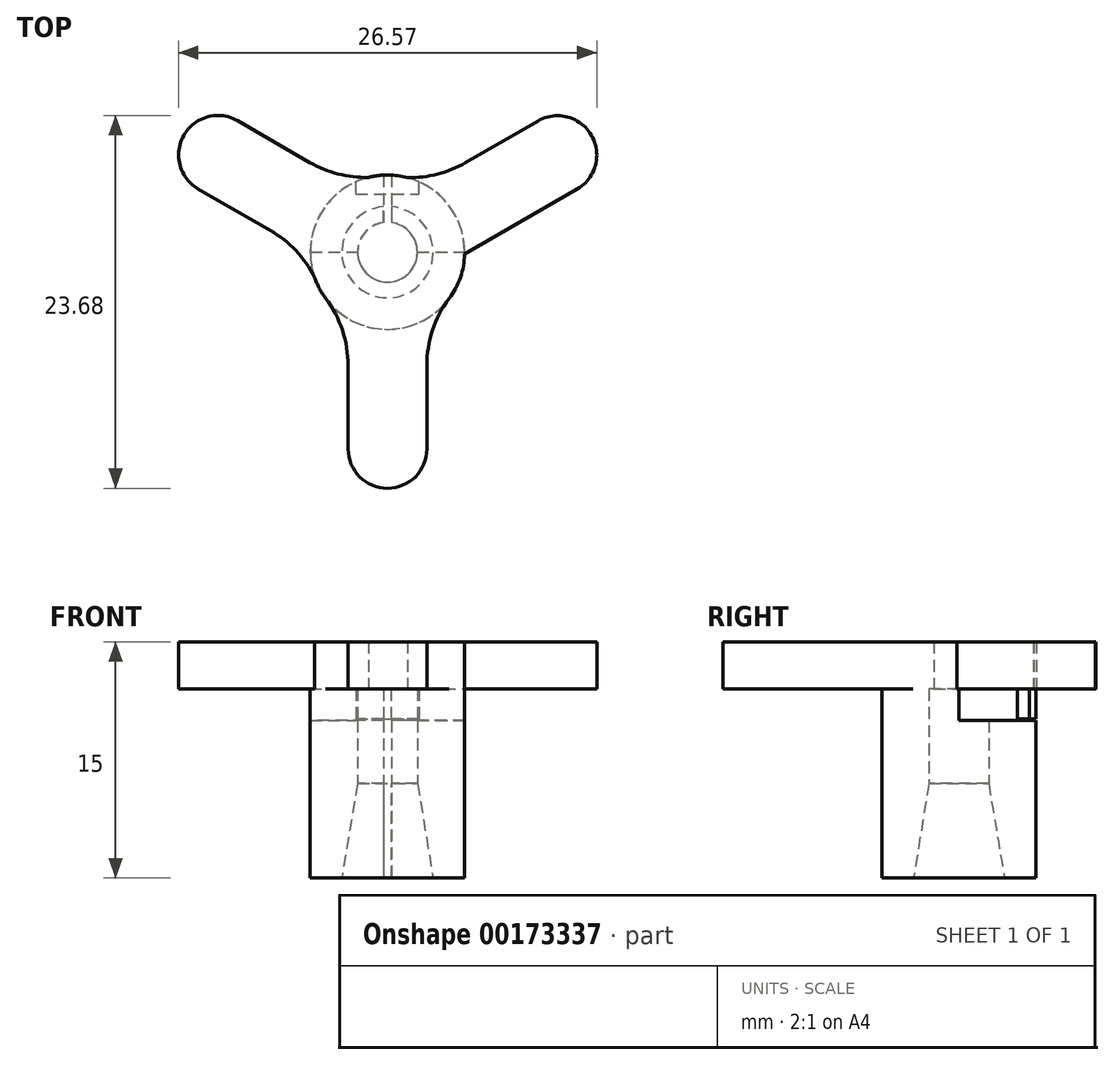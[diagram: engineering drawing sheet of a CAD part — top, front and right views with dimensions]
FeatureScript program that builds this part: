
annotation { "Feature Type Name" : "Feature", "Feature Type Description" : "" }
export const myFeature = defineFeature(function(context is Context, id is Id, definition is map)
    precondition{}
    {
        {
            var Q0;
            Q0=qCreatedBy(makeId("Top.planeOp"),FACE);
            var sketch = newSketch(context, id + "F0", { "sketchPlane" : qUnion([Q0])});
            skCircle(sketch, "E0", {"center": v(0, 0) * mm, "radius": 1.9 * mm});
            skCircle(sketch, "E1", {"center": v(0, 0) * mm, "radius": 4.9 * mm});
            skLineSegment(sketch, "E2", {"start": v(-0.25, 4.9) * mm, "end": v(0.25, 4.9) * mm});
            skPoint(sketch, "E3", {"position": v(0, 4.9) * mm});
            skLineSegment(sketch, "E4", {"start": v(-0.25, 4.9) * mm, "end": v(-0.25, 1.88) * mm});
            skLineSegment(sketch, "E5", {"start": v(0.25, 4.9) * mm, "end": v(0.25, 1.88) * mm});
            skSolve(sketch);
        }
        {
            var Q0;
            {var subQ0=sQuery(id+"F0.wireOp",EDGE,"E4");var subQ1=sQuery(id+"F0.wireOp",EDGE,"E0");var subQ2=makeQuery(id+"F0.imprint","INTERSECT",VERTEX,{"derivedFrom":[subQ1,subQ0]});Q0=makeQuery(id+"F0.imprint","IMPRINT",FACE,{"disambiguationData":[TD([[makeQuery(id+"F0.imprint","IMPRINT",EDGE,{"disambiguationData":[TD([[subQ2,-1.0]])],"derivedFrom":subQ1}),-1.0]])]});}
            extrude(context, id + "F1", {"entities" : qUnion([Q0]), "depth" : 10 * mm});
        }
        {
            var Q0;
            Q0=makeQuery(id+"F1.opExtrude","CAP_FACE",FACE,{"disambiguationData":[OSD([sQuery(id+"F0.wireOp",EDGE,"E0"),sQuery(id+"F0.wireOp",EDGE,"E1"),sQuery(id+"F0.wireOp",EDGE,"E4"),sQuery(id+"F0.wireOp",EDGE,"E5")])],"isStart":false});
            var sketch = newSketch(context, id + "F2", { "sketchPlane" : qUnion([Q0])});
            skArc(sketch, "E6", {"start": v(-4.9, 0) * mm, "mid": v(0, -4.9) * mm, "end": v(4.9, 0) * mm});
            skLineSegment(sketch, "E7", {"start": v(-4.9, 0) * mm, "end": v(4.9, 0) * mm});
            skCircle(sketch, "E8", {"center": v(0, 0) * mm, "radius": 1.9 * mm});
            skSolve(sketch);
        }
        {
            var Q0;
            {var subQ0=sQuery(id+"F2.wireOp",EDGE,"E6");Q0=makeQuery(id+"F2.imprint","IMPRINT",FACE,{"disambiguationData":[TD([[makeQuery(id+"F2.imprint","IMPRINT",EDGE,{"derivedFrom":subQ0}),1.0]])]});}
            extrude(context, id + "F3", {"entities" : qUnion([Q0]), "operationType" : NewBodyOperationType.ADD, "depth" : 2 * mm});
        }
        {
            var Q0;
            Q0=makeQuery(id+"F3.opExtrude","CAP_FACE",FACE,{"disambiguationData":[OSD([sQuery(id+"F2.wireOp",EDGE,"E6"),sQuery(id+"F2.wireOp",EDGE,"E7"),sQuery(id+"F2.wireOp",EDGE,"E8")])],"isStart":false});
            var sketch = newSketch(context, id + "F4", { "sketchPlane" : qUnion([Q0])});
            skCircle(sketch, "E9", {"center": v(0, 0) * mm, "radius": 4.9 * mm});
            skCircle(sketch, "E10", {"center": v(0, 0) * mm, "radius": 15 * mm});
            skArc(sketch, "E11", {"start": v(-2.5, -12.5) * mm, "mid": v(0, -15) * mm, "end": v(2.5, -12.5) * mm});
            skLineSegment(sketch, "E12", {"start": v(-2.5, -12.5) * mm, "end": v(-2.5, -4.21) * mm});
            skLineSegment(sketch, "E13", {"start": v(2.5, -12.5) * mm, "end": v(2.5, -4.21) * mm});
            skArc(sketch, "E14", {"start": v(-2.5, -7.21) * mm, "mid": v(-2.87, -4.96) * mm, "end": v(-3.92, -2.94) * mm});
            skArc(sketch, "E15", {"start": v(3.92, -2.94) * mm, "mid": v(2.87, -4.96) * mm, "end": v(2.5, -7.21) * mm});
            skArc(sketch, "E16.1.0", {"start": v(12.05, 4) * mm, "mid": v(12.96, 7.42) * mm, "end": v(9.55, 8.33) * mm});
            skLineSegment(sketch, "E16.1.1", {"start": v(9.55, 8.33) * mm, "end": v(2.37, 4.19) * mm});
            skLineSegment(sketch, "E16.1.2", {"start": v(12.05, 4) * mm, "end": v(4.87, -0.14) * mm});
            skArc(sketch, "E16.1.3", {"start": v(7.47, 1.36) * mm, "mid": v(5.7, -0.09) * mm, "end": v(4.47, -2.01) * mm});
            skArc(sketch, "E16.1.4", {"start": v(0.55, 4.78) * mm, "mid": v(2.83, 4.88) * mm, "end": v(4.97, 5.69) * mm});
            skArc(sketch, "E16.2.0", {"start": v(-9.52, 8.35) * mm, "mid": v(-12.93, 7.43) * mm, "end": v(-12.02, 4.02) * mm});
            skLineSegment(sketch, "E16.2.1", {"start": v(-12.02, 4.02) * mm, "end": v(-4.84, -0.13) * mm});
            skLineSegment(sketch, "E16.2.2", {"start": v(-9.52, 8.35) * mm, "end": v(-2.34, 4.2) * mm});
            skArc(sketch, "E16.2.3", {"start": v(-4.94, 5.7) * mm, "mid": v(-2.8, 4.9) * mm, "end": v(-0.52, 4.8) * mm});
            skArc(sketch, "E16.2.4", {"start": v(-4.45, -2) * mm, "mid": v(-5.67, -0.07) * mm, "end": v(-7.44, 1.37) * mm});
            skPoint(sketch, "E16.center", {"position": v(0, -0.05) * mm});
            skSolve(sketch);
        }
        {
            var Q0;
            {var subQ6=sQuery(id+"F2.wireOp",EDGE,"E8");Q0=makeQuery(id+"F4.imprint","IMPRINT",FACE,{"disambiguationData":[TD([[makeQuery(id+"F4.imprint","IMPRINT",EDGE,{"derivedFrom":makeQuery(id+"F3.opExtrude","CAP_EDGE",EDGE,{"disambiguationData":[OSD([subQ6])],"isStart":false})}),-1.0]])]});}
            var Q1;
            {var subQ8=sQuery(id+"F2.wireOp",EDGE,"E8");Q1=makeQuery(id+"F4.imprint","IMPRINT",FACE,{"disambiguationData":[TD([[makeQuery(id+"F4.imprint","IMPRINT",EDGE,{"derivedFrom":makeQuery(id+"F3.opExtrude","CAP_EDGE",EDGE,{"disambiguationData":[OSD([subQ8])],"isStart":false})}),1.0]])]});}
            var Q2;
            {var subQ0=sQuery(id+"F4.wireOp",EDGE,"9c31c9c1-0bcc-4ed4-a2f3-30294d7c124c.1.1");Q2=makeQuery(id+"F4.imprint","IMPRINT",FACE,{"disambiguationData":[TD([[makeQuery(id+"F4.imprint","IMPRINT",EDGE,{"derivedFrom":subQ0}),-1.0]])]});}
            var Q3;
            {var subQ0=sQuery(id+"F4.wireOp",EDGE,"9c31c9c1-0bcc-4ed4-a2f3-30294d7c124c.1.0");var subQ1=makeQuery(id+"F4.imprint","INTERSECT",VERTEX,{"derivedFrom":[subQ0,sQuery(id+"F4.wireOp",EDGE,"9c31c9c1-0bcc-4ed4-a2f3-30294d7c124c.1.2")]});Q3=makeQuery(id+"F4.imprint","IMPRINT",FACE,{"disambiguationData":[TD([[makeQuery(id+"F4.imprint","IMPRINT",EDGE,{"disambiguationData":[TD([[subQ1,-1.0]])],"derivedFrom":subQ0}),1.0]])]});}
            var Q4;
            {var subQ0=sQuery(id+"F4.wireOp",EDGE,"STuvLVaa-MU8C-Dhbz-SaFo-3KpY4SZEZLty");var subQ1=makeQuery(id+"F4.imprint","INTERSECT",VERTEX,{"derivedFrom":[subQ0,sQuery(id+"F4.wireOp",EDGE,"ktpVrwZ7-m0nx-2aj5-DfaQ-GeAfub4Ecsry")]});Q4=makeQuery(id+"F4.imprint","IMPRINT",FACE,{"disambiguationData":[TD([[makeQuery(id+"F4.imprint","IMPRINT",EDGE,{"disambiguationData":[TD([[subQ1,-1.0]])],"derivedFrom":subQ0}),1.0]])]});}
            var Q5;
            {var subQ0=sQuery(id+"F4.wireOp",EDGE,"fXAfpD2b-S489-TMEU-ql5s-tNgI2AmWdHs7");Q5=makeQuery(id+"F4.imprint","IMPRINT",FACE,{"disambiguationData":[TD([[makeQuery(id+"F4.imprint","IMPRINT",EDGE,{"derivedFrom":subQ0}),-1.0]])]});}
            var Q6;
            {var subQ0=sQuery(id+"F4.wireOp",EDGE,"9c31c9c1-0bcc-4ed4-a2f3-30294d7c124c.4.1");Q6=makeQuery(id+"F4.imprint","IMPRINT",FACE,{"disambiguationData":[TD([[makeQuery(id+"F4.imprint","IMPRINT",EDGE,{"derivedFrom":subQ0}),-1.0]])]});}
            var Q7;
            {var subQ0=sQuery(id+"F4.wireOp",EDGE,"9c31c9c1-0bcc-4ed4-a2f3-30294d7c124c.4.0");var subQ1=makeQuery(id+"F4.imprint","INTERSECT",VERTEX,{"derivedFrom":[subQ0,sQuery(id+"F4.wireOp",EDGE,"9c31c9c1-0bcc-4ed4-a2f3-30294d7c124c.4.2")]});Q7=makeQuery(id+"F4.imprint","IMPRINT",FACE,{"disambiguationData":[TD([[makeQuery(id+"F4.imprint","IMPRINT",EDGE,{"disambiguationData":[TD([[subQ1,-1.0]])],"derivedFrom":subQ0}),1.0]])]});}
            var Q8;
            {var subQ0=sQuery(id+"F4.wireOp",EDGE,"9c31c9c1-0bcc-4ed4-a2f3-30294d7c124c.3.0");var subQ1=makeQuery(id+"F4.imprint","INTERSECT",VERTEX,{"derivedFrom":[subQ0,sQuery(id+"F4.wireOp",EDGE,"9c31c9c1-0bcc-4ed4-a2f3-30294d7c124c.3.2")]});Q8=makeQuery(id+"F4.imprint","IMPRINT",FACE,{"disambiguationData":[TD([[makeQuery(id+"F4.imprint","IMPRINT",EDGE,{"disambiguationData":[TD([[subQ1,-1.0]])],"derivedFrom":subQ0}),1.0]])]});}
            var Q9;
            {var subQ0=sQuery(id+"F4.wireOp",EDGE,"9c31c9c1-0bcc-4ed4-a2f3-30294d7c124c.2.1");Q9=makeQuery(id+"F4.imprint","IMPRINT",FACE,{"disambiguationData":[TD([[makeQuery(id+"F4.imprint","IMPRINT",EDGE,{"derivedFrom":subQ0}),-1.0]])]});}
            var Q10;
            {var subQ0=sQuery(id+"F4.wireOp",EDGE,"9c31c9c1-0bcc-4ed4-a2f3-30294d7c124c.2.0");var subQ1=makeQuery(id+"F4.imprint","INTERSECT",VERTEX,{"derivedFrom":[subQ0,sQuery(id+"F4.wireOp",EDGE,"9c31c9c1-0bcc-4ed4-a2f3-30294d7c124c.2.2")]});Q10=makeQuery(id+"F4.imprint","IMPRINT",FACE,{"disambiguationData":[TD([[makeQuery(id+"F4.imprint","IMPRINT",EDGE,{"disambiguationData":[TD([[subQ1,-1.0]])],"derivedFrom":subQ0}),1.0]])]});}
            var Q11;
            {var subQ0=sQuery(id+"F4.wireOp",EDGE,"9c31c9c1-0bcc-4ed4-a2f3-30294d7c124c.3.1");Q11=makeQuery(id+"F4.imprint","IMPRINT",FACE,{"disambiguationData":[TD([[makeQuery(id+"F4.imprint","IMPRINT",EDGE,{"derivedFrom":subQ0}),-1.0]])]});}
            var Q12;
            {var subQ4=sQuery(id+"F4.wireOp",EDGE,"45d453c9-bf6c-4dbd-8a0c-38babedebff1.1.0");Q12=makeQuery(id+"F4.imprint","IMPRINT",FACE,{"disambiguationData":[TD([[makeQuery(id+"F4.imprint","IMPRINT",EDGE,{"derivedFrom":subQ4}),-1.0]])]});}
            var Q13;
            {var subQ0=sQuery(id+"F4.wireOp",EDGE,"45d453c9-bf6c-4dbd-8a0c-38babedebff1.1.2");var subQ1=makeQuery(id+"F4.imprint","INTERSECT",VERTEX,{"derivedFrom":[sQuery(id+"F4.wireOp",EDGE,"45d453c9-bf6c-4dbd-8a0c-38babedebff1.1.1"),subQ0]});Q13=makeQuery(id+"F4.imprint","IMPRINT",FACE,{"disambiguationData":[TD([[makeQuery(id+"F4.imprint","IMPRINT",EDGE,{"disambiguationData":[TD([[subQ1,-1.0]])],"derivedFrom":subQ0}),1.0]])]});}
            var Q14;
            {var subQ0=sQuery(id+"F4.wireOp",EDGE,"45d453c9-bf6c-4dbd-8a0c-38babedebff1.4.0");Q14=makeQuery(id+"F4.imprint","IMPRINT",FACE,{"disambiguationData":[TD([[makeQuery(id+"F4.imprint","IMPRINT",EDGE,{"derivedFrom":subQ0}),-1.0]])]});}
            var Q15;
            {var subQ0=sQuery(id+"F4.wireOp",EDGE,"45d453c9-bf6c-4dbd-8a0c-38babedebff1.4.2");var subQ1=makeQuery(id+"F4.imprint","INTERSECT",VERTEX,{"derivedFrom":[sQuery(id+"F4.wireOp",EDGE,"45d453c9-bf6c-4dbd-8a0c-38babedebff1.4.1"),subQ0]});Q15=makeQuery(id+"F4.imprint","IMPRINT",FACE,{"disambiguationData":[TD([[makeQuery(id+"F4.imprint","IMPRINT",EDGE,{"disambiguationData":[TD([[subQ1,-1.0]])],"derivedFrom":subQ0}),1.0]])]});}
            var Q16;
            {var subQ0=sQuery(id+"F4.wireOp",EDGE,"45d453c9-bf6c-4dbd-8a0c-38babedebff1.3.0");Q16=makeQuery(id+"F4.imprint","IMPRINT",FACE,{"disambiguationData":[TD([[makeQuery(id+"F4.imprint","IMPRINT",EDGE,{"derivedFrom":subQ0}),-1.0]])]});}
            var Q17;
            {var subQ0=sQuery(id+"F4.wireOp",EDGE,"45d453c9-bf6c-4dbd-8a0c-38babedebff1.3.2");var subQ1=makeQuery(id+"F4.imprint","INTERSECT",VERTEX,{"derivedFrom":[sQuery(id+"F4.wireOp",EDGE,"45d453c9-bf6c-4dbd-8a0c-38babedebff1.3.1"),subQ0]});Q17=makeQuery(id+"F4.imprint","IMPRINT",FACE,{"disambiguationData":[TD([[makeQuery(id+"F4.imprint","IMPRINT",EDGE,{"disambiguationData":[TD([[subQ1,-1.0]])],"derivedFrom":subQ0}),1.0]])]});}
            var Q18;
            {var subQ0=sQuery(id+"F4.wireOp",EDGE,"45d453c9-bf6c-4dbd-8a0c-38babedebff1.2.0");Q18=makeQuery(id+"F4.imprint","IMPRINT",FACE,{"disambiguationData":[TD([[makeQuery(id+"F4.imprint","IMPRINT",EDGE,{"derivedFrom":subQ0}),-1.0]])]});}
            var Q19;
            {var subQ0=sQuery(id+"F4.wireOp",EDGE,"45d453c9-bf6c-4dbd-8a0c-38babedebff1.2.2");var subQ1=makeQuery(id+"F4.imprint","INTERSECT",VERTEX,{"derivedFrom":[sQuery(id+"F4.wireOp",EDGE,"45d453c9-bf6c-4dbd-8a0c-38babedebff1.2.1"),subQ0]});Q19=makeQuery(id+"F4.imprint","IMPRINT",FACE,{"disambiguationData":[TD([[makeQuery(id+"F4.imprint","IMPRINT",EDGE,{"disambiguationData":[TD([[subQ1,-1.0]])],"derivedFrom":subQ0}),1.0]])]});}
            var Q20;
            {var subQ0=sQuery(id+"F4.wireOp",EDGE,"E16.2.2");var subQ1=sQuery(id+"F4.wireOp",EDGE,"E16.2.0");var subQ2=makeQuery(id+"F4.imprint","INTERSECT",VERTEX,{"derivedFrom":[subQ1,subQ0]});Q20=makeQuery(id+"F4.imprint","IMPRINT",FACE,{"disambiguationData":[TD([[makeQuery(id+"F4.imprint","IMPRINT",EDGE,{"disambiguationData":[TD([[subQ2,-1.0]])],"derivedFrom":subQ1}),1.0]])]});}
            var Q21;
            {var subQ0=sQuery(id+"F4.wireOp",EDGE,"E16.1.2");var subQ1=sQuery(id+"F4.wireOp",EDGE,"E16.1.0");var subQ2=makeQuery(id+"F4.imprint","INTERSECT",VERTEX,{"derivedFrom":[subQ1,subQ0]});Q21=makeQuery(id+"F4.imprint","IMPRINT",FACE,{"disambiguationData":[TD([[makeQuery(id+"F4.imprint","IMPRINT",EDGE,{"disambiguationData":[TD([[subQ2,-1.0]])],"derivedFrom":subQ1}),1.0]])]});}
            var Q22;
            {var subQ5=sQuery(id+"F4.wireOp",EDGE,"E12");var subQ8=sQuery(id+"F4.wireOp",EDGE,"E9");var subQ9=makeQuery(id+"F4.imprint","INTERSECT",VERTEX,{"derivedFrom":[subQ8,subQ5]});Q22=makeQuery(id+"F4.imprint","IMPRINT",FACE,{"disambiguationData":[TD([[makeQuery(id+"F4.imprint","IMPRINT",EDGE,{"disambiguationData":[TD([[subQ9,-1.0]])],"derivedFrom":subQ8}),-1.0]])]});}
            var Q23;
            {var subQ3=sQuery(id+"F4.wireOp",EDGE,"E14");Q23=makeQuery(id+"F4.imprint","IMPRINT",FACE,{"disambiguationData":[TD([[makeQuery(id+"F4.imprint","IMPRINT",EDGE,{"derivedFrom":subQ3}),-1.0]])]});}
            var Q24;
            {var subQ3=sQuery(id+"F4.wireOp",EDGE,"E16.2.4");Q24=makeQuery(id+"F4.imprint","IMPRINT",FACE,{"disambiguationData":[TD([[makeQuery(id+"F4.imprint","IMPRINT",EDGE,{"derivedFrom":subQ3}),-1.0]])]});}
            var Q25;
            {var subQ3=sQuery(id+"F4.wireOp",EDGE,"E15");Q25=makeQuery(id+"F4.imprint","IMPRINT",FACE,{"disambiguationData":[TD([[makeQuery(id+"F4.imprint","IMPRINT",EDGE,{"derivedFrom":subQ3}),-1.0]])]});}
            var Q26;
            {var subQ3=sQuery(id+"F4.wireOp",EDGE,"E16.1.3");Q26=makeQuery(id+"F4.imprint","IMPRINT",FACE,{"disambiguationData":[TD([[makeQuery(id+"F4.imprint","IMPRINT",EDGE,{"derivedFrom":subQ3}),-1.0]])]});}
            var Q27;
            {var subQ3=sQuery(id+"F4.wireOp",EDGE,"E16.2.3");Q27=makeQuery(id+"F4.imprint","IMPRINT",FACE,{"disambiguationData":[TD([[makeQuery(id+"F4.imprint","IMPRINT",EDGE,{"derivedFrom":subQ3}),-1.0]])]});}
            var Q28;
            {var subQ3=sQuery(id+"F4.wireOp",EDGE,"E16.1.4");Q28=makeQuery(id+"F4.imprint","IMPRINT",FACE,{"disambiguationData":[TD([[makeQuery(id+"F4.imprint","IMPRINT",EDGE,{"derivedFrom":subQ3}),-1.0]])]});}
            extrude(context, id + "F5", {"entities" : qUnion([Q0, Q1, Q2, Q3, Q4, Q5, Q6, Q7, Q8, Q9, Q10, Q11, Q12, Q13, Q14, Q15, Q16, Q17, Q18, Q19, Q20, Q21, Q22, Q23, Q24, Q25, Q26, Q27, Q28]), "operationType" : NewBodyOperationType.ADD, "depth" : 3 * mm});
        }
        {
            var Q0;
            Q0=makeQuery(id+"F1.opExtrude","CAP_EDGE",EDGE,{"disambiguationData":[OSD([sQuery(id+"F0.wireOp",EDGE,"E0")])],"isStart":true});
            chamfer(context, id + "F6", {"entities" : qUnion([Q0]), "chamferType" : ChamferType.TWO_OFFSETS, "width1" : 1 * mm, "oppositeDirection" : false, "width2" : 6 * mm, "tangentPropagation" : true});
        }
        {
            var Q0;
            {var subQ1=sQuery(id+"F0.wireOp",EDGE,"E4");var subQ2=sQuery(id+"F0.wireOp",EDGE,"E1");var subQ3=sQuery(id+"F0.wireOp",EDGE,"E0");Q0=makeQuery(id+"F3.boolean.opBoolean","SPLIT",FACE,{"disambiguationData":[TD([makeQuery(id+"F1.opExtrude","SWEPT_FACE",FACE,{"disambiguationData":[OSD([subQ1])]})])],"derivedFrom":makeQuery(id+"F1.opExtrude","CAP_FACE",FACE,{"disambiguationData":[OSD([subQ3,subQ2,subQ1,sQuery(id+"F0.wireOp",EDGE,"E5")])],"isStart":false})});}
            var sketch = newSketch(context, id + "F7", { "sketchPlane" : qUnion([Q0])});
            skLineSegment(sketch, "E17.bottom", {"start": v(-2, 4.9) * mm, "end": v(2, 4.9) * mm});
            skLineSegment(sketch, "E17.top", {"start": v(-2, 3.7) * mm, "end": v(2, 3.7) * mm});
            skLineSegment(sketch, "E17.left", {"start": v(-2, 9.55) * mm, "end": v(-2, 3.7) * mm});
            skLineSegment(sketch, "E17.right", {"start": v(2, 9.55) * mm, "end": v(2, 3.7) * mm});
            skPoint(sketch, "E18", {"position": v(0, 4.9) * mm});
            skPoint(sketch, "E19", {"position": v(-0.25, 4.9) * mm});
            skPoint(sketch, "E20", {"position": v(0.24, 4.9) * mm});
            skArc(sketch, "E21", {"start": v(2, 4.47) * mm, "mid": v(1.14, 4.77) * mm, "end": v(0.24, 4.9) * mm});
            skPoint(sketch, "E22", {"position": v(1.14, 4.77) * mm});
            skSolve(sketch);
        }
        {
            var Q0;
            {var subQ0=sQuery(id+"F7.wireOp",EDGE,"E17.left");var subQ1=sQuery(id+"F7.wireOp",EDGE,"E17.top");var subQ2=makeQuery(id+"F7.imprint","INTERSECT",VERTEX,{"derivedFrom":[subQ1,subQ0]});Q0=makeQuery(id+"F7.imprint","IMPRINT",FACE,{"disambiguationData":[TD([[makeQuery(id+"F7.imprint","IMPRINT",EDGE,{"disambiguationData":[TD([[subQ2,-1.0]])],"derivedFrom":subQ1}),1.0]])]});}
            var Q1;
            {var subQ8=sQuery(id+"F7.wireOp",EDGE,"E17.right");var subQ10=sQuery(id+"F7.wireOp",EDGE,"E17.top");var subQ11=makeQuery(id+"F7.imprint","INTERSECT",VERTEX,{"derivedFrom":[subQ10,subQ8]});Q1=makeQuery(id+"F7.imprint","IMPRINT",FACE,{"disambiguationData":[TD([[makeQuery(id+"F7.imprint","IMPRINT",EDGE,{"disambiguationData":[TD([[subQ11,1.0]])],"derivedFrom":subQ10}),1.0]])]});}
            var Q2;
            {var subQ0=sQuery(id+"F4.wireOp",EDGE,"E14");var subQ1=sQuery(id+"F4.wireOp",EDGE,"E9");var subQ2=sQuery(id+"F4.wireOp",EDGE,"E16.2.4");var subQ3=sQuery(id+"F4.wireOp",EDGE,"E16.1.4");var subQ4=sQuery(id+"F4.wireOp",EDGE,"E16.2.3");var subQ5=sQuery(id+"F4.wireOp",EDGE,"E16.2.0");var subQ11=sQuery(id+"F4.wireOp",EDGE,"E16.1.1");var subQ12=sQuery(id+"F4.wireOp",EDGE,"E16.1.0");var subQ13=sQuery(id+"F4.wireOp",EDGE,"E15");var subQ14=sQuery(id+"F4.wireOp",EDGE,"E16.1.2");var subQ15=sQuery(id+"F4.wireOp",EDGE,"E16.2.1");var subQ16=sQuery(id+"F4.wireOp",EDGE,"E16.2.2");Q2=makeQuery(id+"F5.boolean.opBoolean","SPLIT",FACE,{"disambiguationData":[TD([makeQuery(id+"F1.opExtrude","SWEPT_FACE",FACE,{"disambiguationData":[OSD([sQuery(id+"F0.wireOp",EDGE,"E0")])]})])],"derivedFrom":makeQuery(id+"F5.opExtrude","CAP_FACE",FACE,{"disambiguationData":[OSD([subQ1,sQuery(id+"F4.wireOp",EDGE,"E11"),sQuery(id+"F4.wireOp",EDGE,"E12"),sQuery(id+"F4.wireOp",EDGE,"E13"),subQ0,subQ13,subQ12,subQ11,subQ14,subQ3,subQ5,subQ15,subQ16,subQ4,subQ2])],"isStart":true})});}
            extrude(context, id + "F8", {"entities" : qUnion([Q0, Q1]), "operationType" : NewBodyOperationType.ADD, "endBound" : BoundingType.UP_TO_SURFACE, "endBoundEntityFace" : qUnion([Q2]), "depth" : 25 * mm});
        }
        {
            var Q0;
            Q0=makeQuery(id+"F8.opExtrude","SWEPT_FACE",FACE,{"disambiguationData":[OSD([sQuery(id+"F7.wireOp",EDGE,"E17.bottom")])]});
            var sketch = newSketch(context, id + "F9", { "sketchPlane" : qUnion([Q0])});
            skLineSegment(sketch, "E23.bottom", {"start": v(2, 10.1) * mm, "end": v(-2, 10.1) * mm});
            skLineSegment(sketch, "E23.top", {"start": v(2, 10) * mm, "end": v(-2, 10) * mm});
            skLineSegment(sketch, "E23.left", {"start": v(2, 10.1) * mm, "end": v(2, 10) * mm});
            skLineSegment(sketch, "E23.right", {"start": v(-2, 10.1) * mm, "end": v(-2, 10) * mm});
            skSolve(sketch);
        }
        {
            var Q0;
            {var subQ0=sQuery(id+"F9.wireOp",EDGE,"E23.right");Q0=makeQuery(id+"F9.imprint","IMPRINT",FACE,{"disambiguationData":[TD([[makeQuery(id+"F9.imprint","IMPRINT",EDGE,{"derivedFrom":subQ0}),1.0]])]});}
            var Q1;
            {var subQ0=sQuery(id+"F9.wireOp",EDGE,"E23.bottom");var subQ1=sQuery(id+"F7.wireOp",EDGE,"E17.bottom");var subQ4=makeQuery(id+"F8.opExtrude","SWEPT_EDGE",EDGE,{"disambiguationData":[OSD([subQ1,sQuery(id+"F7.wireOp",EDGE,"E21")])]});var subQ5=makeQuery(id+"F9.imprint","INTERSECT",VERTEX,{"derivedFrom":[subQ4,subQ0]});Q1=makeQuery(id+"F9.imprint","IMPRINT",FACE,{"disambiguationData":[TD([[makeQuery(id+"F9.imprint","IMPRINT",EDGE,{"disambiguationData":[TD([[subQ5,1.0]])],"derivedFrom":subQ0}),1.0]])]});}
            var Q2;
            {var subQ0=sQuery(id+"F9.wireOp",EDGE,"E23.left");Q2=makeQuery(id+"F9.imprint","IMPRINT",FACE,{"disambiguationData":[TD([[makeQuery(id+"F9.imprint","IMPRINT",EDGE,{"derivedFrom":subQ0}),-1.0]])]});}
            extrude(context, id + "F10", {"entities" : qUnion([Q0, Q1, Q2]), "operationType" : NewBodyOperationType.REMOVE, "oppositeDirection" : true, "depth" : 1.5 * mm});
        }
    });
